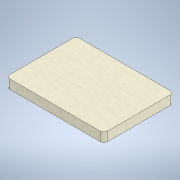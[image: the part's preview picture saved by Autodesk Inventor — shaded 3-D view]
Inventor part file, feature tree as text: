
AUTODESK INVENTOR PART (.ipt)
format: ipt  version: 2021 (Build 250183000, 183)  size: 111,616 bytes
history: native  units: mm
features: extrude x1, sketch x1
ambient origin geometry x8: Origin, YZ Plane, XZ Plane, XY Plane, X Axis, Y Axis, Z Axis, Center Point
bodies: Solid1 (feature_tree)
feature tree (2):
  extrude  "Extrusion1"  Depth=63.0mm
  sketch  "Sketch1"  dims[d0=88.0mm d1=63.0mm d2=3.5mm d3=8.2mm d4=0.0mm]
